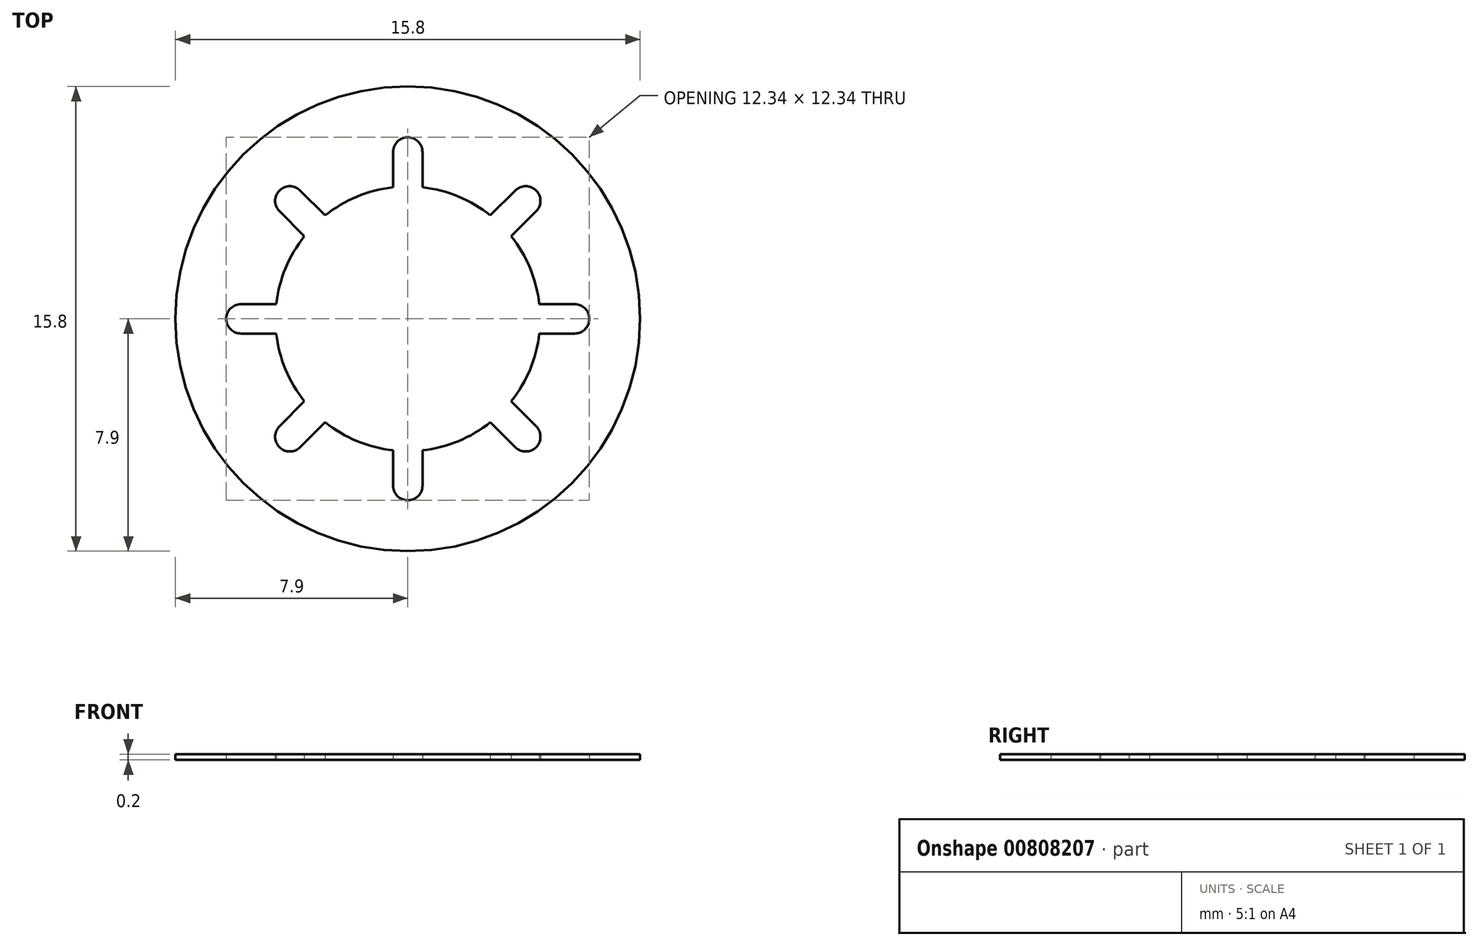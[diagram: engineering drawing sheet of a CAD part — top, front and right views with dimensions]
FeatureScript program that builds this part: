
annotation { "Feature Type Name" : "Feature", "Feature Type Description" : "" }
export const myFeature = defineFeature(function(context is Context, id is Id, definition is map)
    precondition{}
    {
        {
            var Q0;
            Q0=qCreatedBy(makeId("Top.planeOp"),FACE);
            var sketch = newSketch(context, id + "F0", { "sketchPlane" : qUnion([Q0])});
            skCircle(sketch, "E0", {"center": v(0, 0) * mm, "radius": 7.9 * mm});
            skArc(sketch, "E1", {"start": v(-0.5, 4.47) * mm, "mid": v(0, -4.5) * mm, "end": v(0.5, 4.47) * mm});
            skArc(sketch, "E2", {"start": v(-0.5, 5.67) * mm, "mid": v(0, 6.17) * mm, "end": v(0.5, 5.67) * mm});
            skLineSegment(sketch, "E3", {"start": v(-0.5, 5.67) * mm, "end": v(-0.5, 4.47) * mm});
            skLineSegment(sketch, "E4", {"start": v(0.5, 5.67) * mm, "end": v(0.5, 4.47) * mm});
            skLineSegment(sketch, "E5.1.0", {"start": v(-4.36, 3.66) * mm, "end": v(-3.52, 2.8) * mm});
            skArc(sketch, "E5.1.1", {"start": v(-4.36, 3.66) * mm, "mid": v(-4.36, 4.36) * mm, "end": v(-3.66, 4.36) * mm});
            skLineSegment(sketch, "E5.1.2", {"start": v(-3.66, 4.36) * mm, "end": v(-2.8, 3.52) * mm});
            skArc(sketch, "E5.1.3", {"start": v(-3.52, 2.8) * mm, "mid": v(3.18, -3.18) * mm, "end": v(-2.8, 3.52) * mm});
            skLineSegment(sketch, "E5.2.0", {"start": v(-5.67, -0.5) * mm, "end": v(-4.47, -0.5) * mm});
            skArc(sketch, "E5.2.1", {"start": v(-5.67, -0.5) * mm, "mid": v(-6.17, 0) * mm, "end": v(-5.67, 0.5) * mm});
            skLineSegment(sketch, "E5.2.2", {"start": v(-5.67, 0.5) * mm, "end": v(-4.47, 0.5) * mm});
            skArc(sketch, "E5.2.3", {"start": v(-4.47, -0.5) * mm, "mid": v(4.5, 0) * mm, "end": v(-4.47, 0.5) * mm});
            skLineSegment(sketch, "E6.2.3.0", {"start": v(-3.66, -4.36) * mm, "end": v(-2.8, -3.52) * mm});
            skArc(sketch, "E6.3.3.0", {"start": v(-3.66, -4.36) * mm, "mid": v(-4.36, -4.36) * mm, "end": v(-4.36, -3.66) * mm});
            skLineSegment(sketch, "E6.7.3.0", {"start": v(-4.36, -3.66) * mm, "end": v(-3.52, -2.8) * mm});
            skArc(sketch, "E6.10.3.0", {"start": v(-2.8, -3.52) * mm, "mid": v(3.18, 3.18) * mm, "end": v(-3.52, -2.8) * mm});
            skLineSegment(sketch, "E6.2.4.0", {"start": v(0.5, -5.67) * mm, "end": v(0.5, -4.47) * mm});
            skArc(sketch, "E6.3.4.0", {"start": v(0.5, -5.67) * mm, "mid": v(0, -6.17) * mm, "end": v(-0.5, -5.67) * mm});
            skLineSegment(sketch, "E6.7.4.0", {"start": v(-0.5, -5.67) * mm, "end": v(-0.5, -4.47) * mm});
            skArc(sketch, "E6.10.4.0", {"start": v(0.5, -4.47) * mm, "mid": v(0, 4.5) * mm, "end": v(-0.5, -4.47) * mm});
            skLineSegment(sketch, "E6.2.5.0", {"start": v(4.36, -3.66) * mm, "end": v(3.52, -2.8) * mm});
            skArc(sketch, "E6.3.5.0", {"start": v(4.36, -3.66) * mm, "mid": v(4.36, -4.36) * mm, "end": v(3.66, -4.36) * mm});
            skLineSegment(sketch, "E6.7.5.0", {"start": v(3.66, -4.36) * mm, "end": v(2.8, -3.52) * mm});
            skArc(sketch, "E6.10.5.0", {"start": v(3.52, -2.8) * mm, "mid": v(-3.18, 3.18) * mm, "end": v(2.8, -3.52) * mm});
            skLineSegment(sketch, "E6.2.6.0", {"start": v(5.67, 0.5) * mm, "end": v(4.47, 0.5) * mm});
            skArc(sketch, "E6.3.6.0", {"start": v(5.67, 0.5) * mm, "mid": v(6.17, 0) * mm, "end": v(5.67, -0.5) * mm});
            skLineSegment(sketch, "E6.7.6.0", {"start": v(5.67, -0.5) * mm, "end": v(4.47, -0.5) * mm});
            skArc(sketch, "E6.10.6.0", {"start": v(4.47, 0.5) * mm, "mid": v(-4.5, 0) * mm, "end": v(4.47, -0.5) * mm});
            skLineSegment(sketch, "E6.2.7.0", {"start": v(3.66, 4.36) * mm, "end": v(2.8, 3.52) * mm});
            skArc(sketch, "E6.3.7.0", {"start": v(3.66, 4.36) * mm, "mid": v(4.36, 4.36) * mm, "end": v(4.36, 3.66) * mm});
            skLineSegment(sketch, "E6.7.7.0", {"start": v(4.36, 3.66) * mm, "end": v(3.52, 2.8) * mm});
            skArc(sketch, "E6.10.7.0", {"start": v(2.8, 3.52) * mm, "mid": v(-3.18, -3.18) * mm, "end": v(3.52, 2.8) * mm});
            skSolve(sketch);
        }
        {
            var Q0;
            Q0=makeQuery(id+"F0.imprint","IMPRINT",FACE,{"disambiguationData":[TD([[makeQuery(id+"F0.imprint","IMPRINT",EDGE,{"derivedFrom":sQuery(id+"F0.wireOp",EDGE,"E0")}),1.0]])]});
            extrude(context, id + "F1", {"entities" : qUnion([Q0]), "depth" : 0.2 * mm, "offsetDistance" : 25 * mm});
        }
    });
